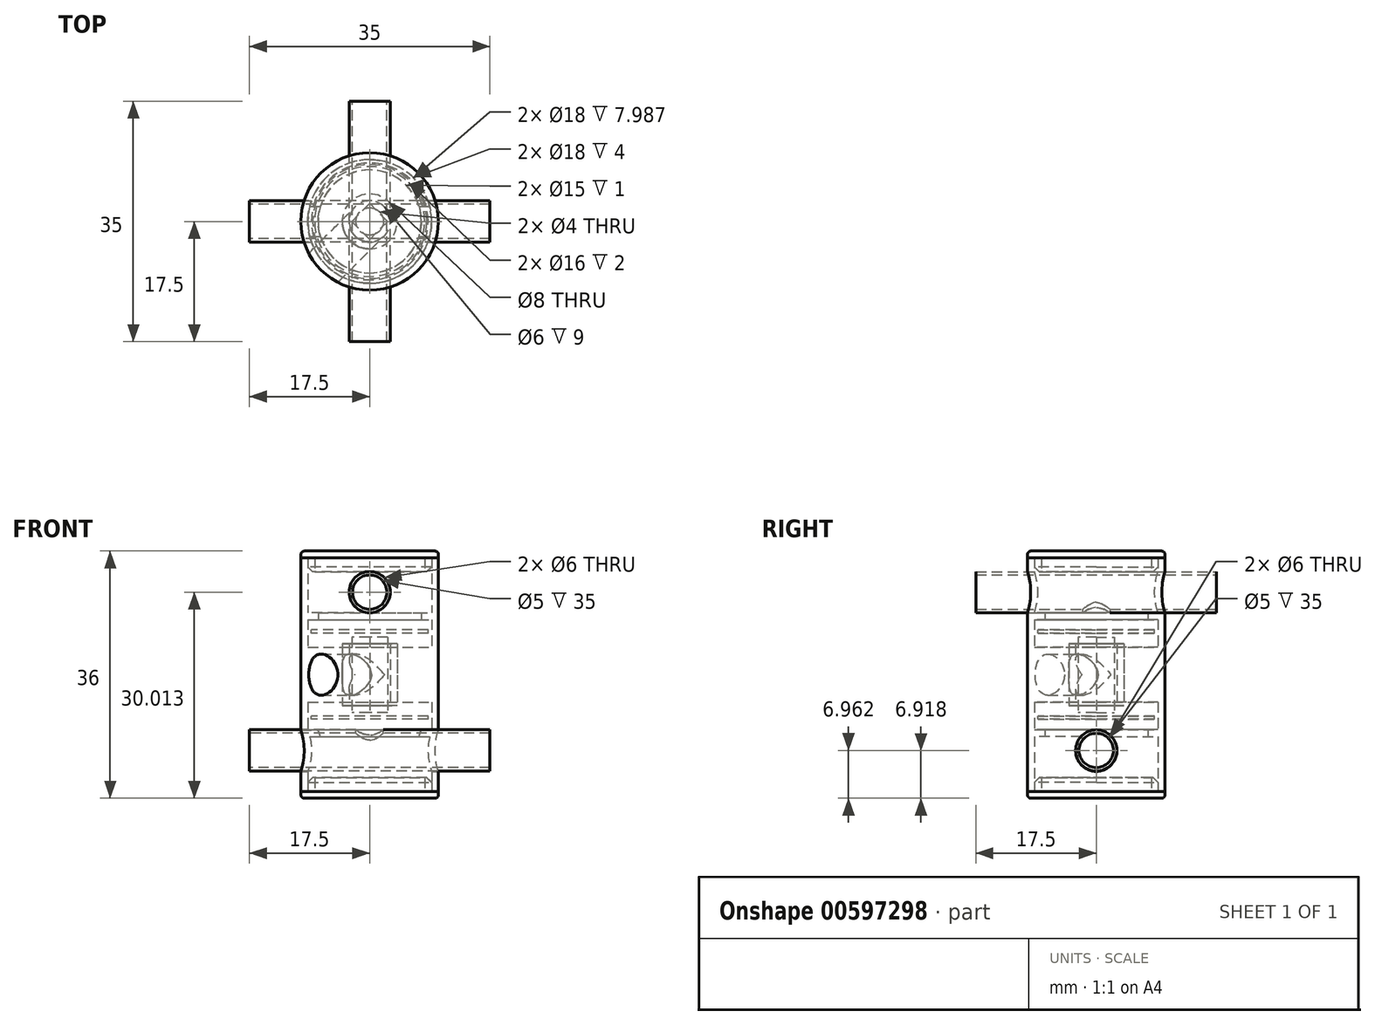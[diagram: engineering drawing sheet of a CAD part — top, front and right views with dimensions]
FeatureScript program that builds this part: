
annotation { "Feature Type Name" : "Feature", "Feature Type Description" : "" }
export const myFeature = defineFeature(function(context is Context, id is Id, definition is map)
    precondition{}
    {
        {
            var Q0;
            Q0=qCreatedBy(makeId("Front.planeOp"),FACE);
            var sketch = newSketch(context, id + "F0", { "sketchPlane" : qUnion([Q0])});
            skLineSegment(sketch, "E0.top", {"start": v(0, 15) * mm, "end": v(-30, 15) * mm});
            skLineSegment(sketch, "E1", {"start": v(0, 30) * mm, "end": v(0, 36) * mm});
            skLineSegment(sketch, "E2", {"start": v(0, 0) * mm, "end": v(0, -6) * mm});
            skSolve(sketch);
        }
        {
            var Q0;
            Q0=qCreatedBy(makeId("Front.planeOp"),FACE);
            var sketch = newSketch(context, id + "F1", { "sketchPlane" : qUnion([Q0])});
            skLineSegment(sketch, "E3.bottom", {"start": v(4, 19.01) * mm, "end": v(9, 19.01) * mm});
            skLineSegment(sketch, "E3.top", {"start": v(4, 10.99) * mm, "end": v(9, 10.99) * mm});
            skLineSegment(sketch, "E3.left", {"start": v(4, 19.01) * mm, "end": v(4, 10.99) * mm});
            skLineSegment(sketch, "E3.right", {"start": v(9, 19.01) * mm, "end": v(9, 10.99) * mm});
            skLineSegment(sketch, "E4.bottom", {"start": v(9, 32) * mm, "end": v(10, 32) * mm});
            skLineSegment(sketch, "E4.top", {"start": v(9, -2) * mm, "end": v(10, -2) * mm});
            skLineSegment(sketch, "E4.left", {"start": v(9, 32) * mm, "end": v(9, -2) * mm});
            skLineSegment(sketch, "E4.right", {"start": v(10, 32) * mm, "end": v(10, -2) * mm});
            skLineSegment(sketch, "E5.bottom", {"start": v(7.5, 24.01) * mm, "end": v(9, 24.01) * mm});
            skLineSegment(sketch, "E5.top", {"start": v(7.5, 23.01) * mm, "end": v(9, 23.01) * mm});
            skLineSegment(sketch, "E5.left", {"start": v(7.5, 24.01) * mm, "end": v(7.5, 23.01) * mm});
            skLineSegment(sketch, "E6", {"start": v(9, 24.01) * mm, "end": v(9, 23.01) * mm});
            skLineSegment(sketch, "E7.MirrorCS", {"start": v(7.5, 6.99) * mm, "end": v(9, 6.99) * mm});
            skLineSegment(sketch, "E8.MirrorCS", {"start": v(7.5, 5.99) * mm, "end": v(7.5, 6.99) * mm});
            skLineSegment(sketch, "E9.MirrorCS", {"start": v(9, 5.99) * mm, "end": v(9, 6.99) * mm});
            skLineSegment(sketch, "E10.MirrorCS", {"start": v(7.5, 5.99) * mm, "end": v(9, 5.99) * mm});
            skSolve(sketch);
        }
        {
            var Q0;
            Q0=qCreatedBy(makeId("Front.planeOp"),FACE);
            var sketch = newSketch(context, id + "F2", { "sketchPlane" : qUnion([Q0])});
            skLineSegment(sketch, "E11.bottom", {"start": v(0, 21.51) * mm, "end": v(8.5, 21.51) * mm});
            skLineSegment(sketch, "E11.top", {"start": v(0, 21.01) * mm, "end": v(8.5, 21.01) * mm});
            skLineSegment(sketch, "E11.left", {"start": v(0, 21.51) * mm, "end": v(0, 21.01) * mm});
            skLineSegment(sketch, "E11.right", {"start": v(8.5, 21.51) * mm, "end": v(8.5, 21.01) * mm});
            skLineSegment(sketch, "E12.MirrorCS", {"start": v(0, 8.99) * mm, "end": v(8.5, 8.99) * mm});
            skLineSegment(sketch, "E13.MirrorCS", {"start": v(0, 8.49) * mm, "end": v(8.5, 8.49) * mm});
            skLineSegment(sketch, "E14.MirrorCS", {"start": v(0, 8.49) * mm, "end": v(0, 8.99) * mm});
            skLineSegment(sketch, "E15.MirrorCS", {"start": v(8.5, 8.49) * mm, "end": v(8.5, 8.99) * mm});
            skSolve(sketch);
        }
        {
            var Q0;
            Q0=makeQuery(id+"F2.imprint","IMPRINT",FACE,{"disambiguationData":[TD([[makeQuery(id+"F2.imprint","IMPRINT",EDGE,{"derivedFrom":sQuery(id+"F2.wireOp",EDGE,"E12.MirrorCS")}),-1.0]])]});
            var Q1;
            Q1=makeQuery(id+"F2.imprint","IMPRINT",FACE,{"disambiguationData":[TD([[makeQuery(id+"F2.imprint","IMPRINT",EDGE,{"derivedFrom":sQuery(id+"F2.wireOp",EDGE,"E11.bottom")}),-1.0]])]});
            var Q2;
            Q2=sQuery(id+"F2.wireOp",EDGE,"E11.left");
            revolve(context, id + "F3", {"entities" : qUnion([Q0, Q1]), "axis" : qUnion([Q2]), "revolveType" : RevolveType.FULL});
        }
        {
            var Q0;
            Q0 = qSketchRegion(id + "F1", true);
            var Q1;
            Q1=sQuery(id+"F0.wireOp",EDGE,"E1");
            revolve(context, id + "F4", {"entities" : qUnion([Q0]), "axis" : qUnion([Q1]), "revolveType" : RevolveType.FULL});
        }
        {
            var Q0;
            Q0=qCreatedBy(makeId("Front.planeOp"),FACE);
            var sketch = newSketch(context, id + "F5", { "sketchPlane" : qUnion([Q0])});
            skCircle(sketch, "E16", {"center": v(0, 27.01) * mm, "radius": 3 * mm});
            skLineSegment(sketch, "E17.bottom", {"start": v(4, 10.51) * mm, "end": v(3, 10.51) * mm});
            skLineSegment(sketch, "E17.top", {"start": v(4, 19.51) * mm, "end": v(3, 19.51) * mm});
            skLineSegment(sketch, "E17.left", {"start": v(4, 10.51) * mm, "end": v(4, 19.51) * mm});
            skLineSegment(sketch, "E17.right", {"start": v(3, 10.51) * mm, "end": v(3, 19.51) * mm});
            skPoint(sketch, "E17.middle", {"position": v(0, 15.01) * mm});
            skSolve(sketch);
        }
        {
            var Q0;
            Q0=makeQuery(id+"F5.imprint","IMPRINT",FACE,{"disambiguationData":[TD([[makeQuery(id+"F5.imprint","IMPRINT",EDGE,{"derivedFrom":sQuery(id+"F5.wireOp",EDGE,"E16")}),1.0]])]});
            extrude(context, id + "F6", {"entities" : qUnion([Q0]), "operationType" : NewBodyOperationType.REMOVE, "endBound" : BoundingType.SYMMETRIC, "depth" : 25 * mm, "offsetDistance" : 25 * mm});
        }
        {
            var Q0;
            Q0=makeQuery(id+"F5.imprint","IMPRINT",FACE,{"disambiguationData":[TD([[makeQuery(id+"F5.imprint","IMPRINT",EDGE,{"derivedFrom":sQuery(id+"F5.wireOp",EDGE,"E17.bottom")}),-1.0]])]});
            var Q1;
            Q1=sQuery(id+"F0.wireOp",EDGE,"E1");
            revolve(context, id + "F7", {"entities" : qUnion([Q0]), "axis" : qUnion([Q1]), "revolveType" : RevolveType.FULL});
        }
        {
            var Q0;
            Q0=makeQuery(id+"F3.opRevolve","SWEPT_FACE",FACE,{"disambiguationData":[OSD([sQuery(id+"F2.wireOp",EDGE,"E12.MirrorCS")])]});
            var sketch = newSketch(context, id + "F8", { "sketchPlane" : qUnion([Q0])});
            skSolve(sketch);
        }
        {
            var Q0;
            Q0=makeQuery(id+"F8.imprint","IMPRINT",FACE,{"disambiguationData":[TD([[makeQuery(id+"F8.imprint","IMPRINT",EDGE,{"derivedFrom":makeQuery(id+"F3.opRevolve","SWEPT_EDGE",EDGE,{"disambiguationData":[OSD([sQuery(id+"F2.wireOp",EDGE,"E12.MirrorCS"),sQuery(id+"F2.wireOp",EDGE,"E15.MirrorCS")])]})}),1.0]])]});
            var sketch = newSketch(context, id + "F9", { "sketchPlane" : qUnion([Q0])});
            skLineSegment(sketch, "E18.bottom", {"start": v(-16.44, -8.27) * mm, "end": v(-23.88, -8.27) * mm});
            skLineSegment(sketch, "E18.top", {"start": v(-16.44, -1.54) * mm, "end": v(-23.88, -1.54) * mm});
            skLineSegment(sketch, "E18.left", {"start": v(-16.44, -8.27) * mm, "end": v(-16.44, -1.54) * mm});
            skLineSegment(sketch, "E18.right", {"start": v(-23.88, -8.27) * mm, "end": v(-23.88, -1.54) * mm});
            skPoint(sketch, "E18.middle", {"position": v(-20.16, -4.9) * mm});
            skSolve(sketch);
        }
        {
            var Q0;
            Q0 = qSketchRegion(id + "F9", true);
            extrude(context, id + "F10", {"entities" : qUnion([Q0]), "depth" : 0.5 * mm, "offsetDistance" : 25 * mm});
        }
        {
            var Q0;
            Q0=makeQuery(id+"F10.opExtrude","CAP_FACE",FACE,{"disambiguationData":[OSD([sQuery(id+"F9.wireOp",EDGE,"E18.bottom"),sQuery(id+"F9.wireOp",EDGE,"E18.top"),sQuery(id+"F9.wireOp",EDGE,"E18.left"),sQuery(id+"F9.wireOp",EDGE,"E18.right")])],"isStart":false});
            var sketch = newSketch(context, id + "F11", { "sketchPlane" : qUnion([Q0])});
            skLineSegment(sketch, "E19.bottom", {"start": v(1.85, -1.85) * mm, "end": v(-1.85, -1.85) * mm});
            skLineSegment(sketch, "E19.top", {"start": v(1.85, 1.85) * mm, "end": v(-1.85, 1.85) * mm});
            skLineSegment(sketch, "E19.left", {"start": v(1.85, -1.85) * mm, "end": v(1.85, 1.85) * mm});
            skLineSegment(sketch, "E19.right", {"start": v(-1.85, -1.85) * mm, "end": v(-1.85, 1.85) * mm});
            skPoint(sketch, "E19.middle", {"position": v(0, 0) * mm});
            skSolve(sketch);
        }
        {
            var Q0;
            Q0=makeQuery(id+"F11.imprint","IMPRINT",FACE,{"disambiguationData":[TD([[makeQuery(id+"F11.imprint","IMPRINT",EDGE,{"derivedFrom":sQuery(id+"F11.wireOp",EDGE,"E19.bottom")}),-1.0]])]});
            extrude(context, id + "F12", {"entities" : qUnion([Q0]), "operationType" : NewBodyOperationType.ADD, "depth" : 11 * mm, "offsetDistance" : 25 * mm});
        }
        {
            var Q0;
            Q0=makeQuery(id+"F10.opExtrude","SWEPT_BODY",BODY,{"disambiguationData":[OSD([sQuery(id+"F9.wireOp",EDGE,"E18.bottom"),sQuery(id+"F9.wireOp",EDGE,"E18.top"),sQuery(id+"F9.wireOp",EDGE,"E18.left"),sQuery(id+"F9.wireOp",EDGE,"E18.right")])]});
            deleteBodies(context, id + "F13", {"entities" : qUnion([Q0])});
        }
        {
            var Q0;
            Q0=qCreatedBy(makeId("Right.planeOp"),FACE);
            var sketch = newSketch(context, id + "F14", { "sketchPlane" : qUnion([Q0])});
            skCircle(sketch, "E20", {"center": v(0, 3.92) * mm, "radius": 3 * mm});
            skSolve(sketch);
        }
        {
            var Q0;
            Q0=makeQuery(id+"F14.imprint","IMPRINT",FACE,{"disambiguationData":[TD([[makeQuery(id+"F14.imprint","IMPRINT",EDGE,{"derivedFrom":sQuery(id+"F14.wireOp",EDGE,"E20")}),1.0]])]});
            extrude(context, id + "F15", {"entities" : qUnion([Q0]), "operationType" : NewBodyOperationType.REMOVE, "endBound" : BoundingType.SYMMETRIC, "oppositeDirection" : true, "depth" : 125 * mm, "offsetDistance" : 25 * mm});
        }
        {
            var Q0;
            Q0=makeQuery(id+"F12.opExtrude","SWEPT_BODY",BODY,{"disambiguationData":[OSD([sQuery(id+"F11.wireOp",EDGE,"E19.bottom"),sQuery(id+"F11.wireOp",EDGE,"E19.top"),sQuery(id+"F11.wireOp",EDGE,"E19.left"),sQuery(id+"F11.wireOp",EDGE,"E19.right")])]});
            var Q1;
            Q1=sQuery(id+"F0.wireOp",EDGE,"E1");
            transform(context, id + "F16", {"entities" : qUnion([Q0]), "transformType" : TransformType.ROTATION, "transformAxis" : qUnion([Q1]), "angle" : 45 * degree, "makeCopy" : false});
        }
        {
            var Q0;
            Q0=makeQuery(id+"F7.opRevolve","SWEPT_BODY",BODY,{"disambiguationData":[OSD([sQuery(id+"F5.wireOp",EDGE,"E17.bottom"),sQuery(id+"F5.wireOp",EDGE,"E17.top"),sQuery(id+"F5.wireOp",EDGE,"E17.left"),sQuery(id+"F5.wireOp",EDGE,"E17.right")])]});
            var Q1;
            Q1=sQuery(id+"F0.wireOp",EDGE,"E1");
            transform(context, id + "F17", {"entities" : qUnion([Q0]), "transformType" : TransformType.ROTATION, "transformAxis" : qUnion([Q1]), "angle" : 45 * degree, "oppositeDirection" : true, "makeCopy" : false});
        }
        {
            var Q0;
            Q0=makeQuery(id+"F12.opExtrude","SWEPT_FACE",FACE,{"disambiguationData":[OSD([sQuery(id+"F11.wireOp",EDGE,"E19.right")])]});
            var sketch = newSketch(context, id + "F18", { "sketchPlane" : qUnion([Q0])});
            skCircle(sketch, "E21", {"center": v(0, 15) * mm, "radius": 3 * mm});
            skSolve(sketch);
        }
        {
            var Q0;
            {var subQ0=sQuery(id+"F18.wireOp",EDGE,"E21");var subQ1=makeQuery(id+"F12.opExtrude","SWEPT_EDGE",EDGE,{"disambiguationData":[OSD([sQuery(id+"F11.wireOp",EDGE,"E19.top"),sQuery(id+"F11.wireOp",EDGE,"E19.right")])]});var subQ2=makeQuery(id+"F18.imprint","INTERSECT",VERTEX,{"disambiguationData":[OD(0.0)],"derivedFrom":[subQ1,subQ0]});Q0=makeQuery(id+"F18.imprint","IMPRINT",FACE,{"disambiguationData":[TD([[makeQuery(id+"F18.imprint","IMPRINT",EDGE,{"disambiguationData":[TD([[subQ2,-1.0]])],"derivedFrom":subQ0}),1.0]])]});}
            var Q1;
            {var subQ0=sQuery(id+"F18.wireOp",EDGE,"E21");var subQ1=sQuery(id+"F11.wireOp",EDGE,"E19.right");var subQ2=makeQuery(id+"F12.opExtrude","SWEPT_EDGE",EDGE,{"disambiguationData":[OSD([sQuery(id+"F11.wireOp",EDGE,"E19.top"),subQ1])]});var subQ3=makeQuery(id+"F18.imprint","INTERSECT",VERTEX,{"disambiguationData":[OD(0.0)],"derivedFrom":[subQ2,subQ0]});Q1=makeQuery(id+"F18.imprint","IMPRINT",FACE,{"disambiguationData":[TD([[makeQuery(id+"F18.imprint","IMPRINT",EDGE,{"disambiguationData":[TD([[subQ3,1.0]])],"derivedFrom":subQ0}),1.0]])]});}
            var Q2;
            {var subQ0=sQuery(id+"F18.wireOp",EDGE,"E21");var subQ1=makeQuery(id+"F12.opExtrude","SWEPT_EDGE",EDGE,{"disambiguationData":[OSD([sQuery(id+"F11.wireOp",EDGE,"E19.bottom"),sQuery(id+"F11.wireOp",EDGE,"E19.right")])]});var subQ2=makeQuery(id+"F18.imprint","INTERSECT",VERTEX,{"disambiguationData":[OD(0.0)],"derivedFrom":[subQ1,subQ0]});Q2=makeQuery(id+"F18.imprint","IMPRINT",FACE,{"disambiguationData":[TD([[makeQuery(id+"F18.imprint","IMPRINT",EDGE,{"disambiguationData":[TD([[subQ2,1.0]])],"derivedFrom":subQ0}),1.0]])]});}
            extrude(context, id + "F19", {"entities" : qUnion([Q0, Q1, Q2]), "operationType" : NewBodyOperationType.REMOVE, "depth" : 25 * mm, "offsetDistance" : 25 * mm});
        }
        {
            var Q0;
            Q0=makeQuery(id+"F19.boolean.opBoolean","COPY",FACE,{"disambiguationData":[OD(0.0)],"derivedFrom":makeQuery(id+"F19.opExtrude","CAP_FACE",FACE,{"disambiguationData":[OSD([sQuery(id+"F18.wireOp",EDGE,"E21")])],"isStart":true})});
            var Q1;
            Q1=makeQuery(id+"F19.boolean.opBoolean","COPY",FACE,{"disambiguationData":[OD(1.0)],"derivedFrom":makeQuery(id+"F19.opExtrude","CAP_FACE",FACE,{"disambiguationData":[OSD([sQuery(id+"F18.wireOp",EDGE,"E21")])],"isStart":true})});
            extrude(context, id + "F20", {"entities" : qUnion([Q0, Q1]), "operationType" : NewBodyOperationType.REMOVE, "oppositeDirection" : true, "depth" : 1.8 * mm, "offsetDistance" : 25 * mm});
        }
        {
            var Q0;
            {var subQ0=sQuery(id+"F18.wireOp",EDGE,"E21");var subQ1=sQuery(id+"F11.wireOp",EDGE,"E19.right");var subQ2=makeQuery(id+"F12.opExtrude","SWEPT_EDGE",EDGE,{"disambiguationData":[OSD([sQuery(id+"F11.wireOp",EDGE,"E19.top"),subQ1])]});var subQ3=makeQuery(id+"F18.imprint","INTERSECT",VERTEX,{"disambiguationData":[OD(0.0)],"derivedFrom":[subQ2,subQ0]});Q0=makeQuery(id+"F18.imprint","IMPRINT",FACE,{"disambiguationData":[TD([[makeQuery(id+"F18.imprint","IMPRINT",EDGE,{"disambiguationData":[TD([[subQ3,1.0]])],"derivedFrom":subQ0}),1.0]])]});}
            var Q1;
            {var subQ0=sQuery(id+"F18.wireOp",EDGE,"E21");var subQ1=makeQuery(id+"F12.opExtrude","SWEPT_EDGE",EDGE,{"disambiguationData":[OSD([sQuery(id+"F11.wireOp",EDGE,"E19.top"),sQuery(id+"F11.wireOp",EDGE,"E19.right")])]});var subQ2=makeQuery(id+"F18.imprint","INTERSECT",VERTEX,{"disambiguationData":[OD(0.0)],"derivedFrom":[subQ1,subQ0]});Q1=makeQuery(id+"F18.imprint","IMPRINT",FACE,{"disambiguationData":[TD([[makeQuery(id+"F18.imprint","IMPRINT",EDGE,{"disambiguationData":[TD([[subQ2,-1.0]])],"derivedFrom":subQ0}),1.0]])]});}
            var Q2;
            {var subQ0=sQuery(id+"F18.wireOp",EDGE,"E21");var subQ1=makeQuery(id+"F12.opExtrude","SWEPT_EDGE",EDGE,{"disambiguationData":[OSD([sQuery(id+"F11.wireOp",EDGE,"E19.bottom"),sQuery(id+"F11.wireOp",EDGE,"E19.right")])]});var subQ2=makeQuery(id+"F18.imprint","INTERSECT",VERTEX,{"disambiguationData":[OD(0.0)],"derivedFrom":[subQ1,subQ0]});Q2=makeQuery(id+"F18.imprint","IMPRINT",FACE,{"disambiguationData":[TD([[makeQuery(id+"F18.imprint","IMPRINT",EDGE,{"disambiguationData":[TD([[subQ2,1.0]])],"derivedFrom":subQ0}),1.0]])]});}
            extrude(context, id + "F21", {"entities" : qUnion([Q0, Q1, Q2]), "operationType" : NewBodyOperationType.REMOVE, "depth" : 25 * mm, "offsetDistance" : 25 * mm});
        }
        {
            var Q0;
            Q0=qCreatedBy(makeId("Front.planeOp"),FACE);
            var sketch = newSketch(context, id + "F22", { "sketchPlane" : qUnion([Q0])});
            skLineSegment(sketch, "E22.top", {"start": v(10, 33) * mm, "end": v(0, 33) * mm});
            skLineSegment(sketch, "E22.left", {"start": v(10, 32) * mm, "end": v(10, 33) * mm});
            skLineSegment(sketch, "E22.right", {"start": v(0, 32) * mm, "end": v(0, 33) * mm});
            skLineSegment(sketch, "E23.top", {"start": v(9, 30) * mm, "end": v(8, 30) * mm});
            skLineSegment(sketch, "E23.left", {"start": v(9, 32) * mm, "end": v(9, 30) * mm});
            skLineSegment(sketch, "E23.right", {"start": v(8, 32) * mm, "end": v(8, 30) * mm});
            skLineSegment(sketch, "E24", {"start": v(8, 32) * mm, "end": v(0, 32) * mm});
            skLineSegment(sketch, "E25", {"start": v(9, 32) * mm, "end": v(10, 32) * mm});
            skLineSegment(sketch, "E26.MirrorCS", {"start": v(9, -2) * mm, "end": v(10, -2) * mm});
            skLineSegment(sketch, "E27.MirrorCS", {"start": v(10, -2) * mm, "end": v(10, -3) * mm});
            skLineSegment(sketch, "E28.MirrorCS", {"start": v(9, 0) * mm, "end": v(8, 0) * mm});
            skLineSegment(sketch, "E29.MirrorCS", {"start": v(0, -2) * mm, "end": v(0, -3) * mm});
            skLineSegment(sketch, "E30.MirrorCS", {"start": v(10, -3) * mm, "end": v(0, -3) * mm});
            skLineSegment(sketch, "E31.MirrorCS", {"start": v(8, -2) * mm, "end": v(8, 0) * mm});
            skLineSegment(sketch, "E32.MirrorCS", {"start": v(8, -2) * mm, "end": v(0, -2) * mm});
            skLineSegment(sketch, "E33.MirrorCS", {"start": v(9, -2) * mm, "end": v(9, 0) * mm});
            skSolve(sketch);
        }
        {
            var Q0;
            Q0=makeQuery(id+"F22.imprint","IMPRINT",FACE,{"disambiguationData":[TD([[makeQuery(id+"F22.imprint","IMPRINT",EDGE,{"derivedFrom":sQuery(id+"F22.wireOp",EDGE,"E22.top")}),1.0]])]});
            var Q1;
            Q1=makeQuery(id+"F22.imprint","IMPRINT",FACE,{"disambiguationData":[TD([[makeQuery(id+"F22.imprint","IMPRINT",EDGE,{"derivedFrom":sQuery(id+"F22.wireOp",EDGE,"E26.MirrorCS")}),-1.0]])]});
            var Q2;
            Q2=sQuery(id+"F0.wireOp",EDGE,"E1");
            revolve(context, id + "F23", {"entities" : qUnion([Q0, Q1]), "axis" : qUnion([Q2]), "revolveType" : RevolveType.FULL});
        }
        {
            var Q0;
            Q0=makeQuery(id+"F23.opRevolve","SWEPT_EDGE",EDGE,{"disambiguationData":[OSD([sQuery(id+"F22.wireOp",EDGE,"E22.top"),sQuery(id+"F22.wireOp",EDGE,"E22.left")])]});
            var Q1;
            Q1=makeQuery(id+"F23.opRevolve","SWEPT_EDGE",EDGE,{"disambiguationData":[OSD([sQuery(id+"F22.wireOp",EDGE,"E27.MirrorCS"),sQuery(id+"F22.wireOp",EDGE,"E30.MirrorCS")])]});
            fillet(context, id + "F24", {"entities" : qUnion([Q0, Q1]), "radius" : 0.5 * mm, "tangentPropagation" : true, "allowEdgeOverflow" : false});
        }
        {
            var Q0;
            Q0=makeQuery(id+"F23.opRevolve","SWEPT_EDGE",EDGE,{"disambiguationData":[OSD([sQuery(id+"F22.wireOp",EDGE,"E23.top"),sQuery(id+"F22.wireOp",EDGE,"E23.left")])]});
            var Q1;
            Q1=makeQuery(id+"F23.opRevolve","SWEPT_EDGE",EDGE,{"disambiguationData":[OSD([sQuery(id+"F22.wireOp",EDGE,"E28.MirrorCS"),sQuery(id+"F22.wireOp",EDGE,"E33.MirrorCS")])]});
            chamfer(context, id + "F25", {"entities" : qUnion([Q0, Q1]), "width" : 0.7 * mm, "tangentPropagation" : true});
        }
        {
            var Q0;
            Q0=qCreatedBy(makeId("Front.planeOp"),FACE);
            var sketch = newSketch(context, id + "F26", { "sketchPlane" : qUnion([Q0])});
            skCircle(sketch, "E34", {"center": v(0, 27.01) * mm, "radius": 3 * mm});
            skCircle(sketch, "E35", {"center": v(0, 27.01) * mm, "radius": 2.5 * mm});
            skSolve(sketch);
        }
        {
            var Q0;
            Q0=makeQuery(id+"F26.imprint","IMPRINT",FACE,{"disambiguationData":[TD([[makeQuery(id+"F26.imprint","IMPRINT",EDGE,{"derivedFrom":sQuery(id+"F26.wireOp",EDGE,"E34")}),1.0]])]});
            extrude(context, id + "F27", {"entities" : qUnion([Q0]), "endBound" : BoundingType.SYMMETRIC, "depth" : 35 * mm, "offsetDistance" : 25 * mm});
        }
        {
            var Q0;
            Q0=makeQuery(id+"F3.opRevolve","SWEPT_FACE",FACE,{"disambiguationData":[OSD([sQuery(id+"F2.wireOp",EDGE,"E11.bottom")])]});
            var sketch = newSketch(context, id + "F28", { "sketchPlane" : qUnion([Q0])});
            skCircle(sketch, "E36", {"center": v(0, 0) * mm, "radius": 2 * mm});
            skSolve(sketch);
        }
        {
            var Q0;
            Q0=makeQuery(id+"F28.imprint","IMPRINT",FACE,{"disambiguationData":[TD([[makeQuery(id+"F28.imprint","IMPRINT",EDGE,{"derivedFrom":sQuery(id+"F28.wireOp",EDGE,"E36")}),1.0]])]});
            extrude(context, id + "F29", {"entities" : qUnion([Q0]), "operationType" : NewBodyOperationType.REMOVE, "depth" : 5 * mm, "offsetDistance" : 25 * mm});
        }
        {
            var Q0;
            Q0=makeQuery(id+"F27.opExtrude","SWEPT_BODY",BODY,{"disambiguationData":[OSD([sQuery(id+"F26.wireOp",EDGE,"E34"),sQuery(id+"F26.wireOp",EDGE,"E35")])]});
            var Q1;
            Q1=makeQuery(id+"F3.opRevolve","SWEPT_FACE",FACE,{"disambiguationData":[OSD([sQuery(id+"F2.wireOp",EDGE,"E13.MirrorCS")])]});
            mirror(context, id + "F30", {"entities" : qUnion([Q0]), "mirrorPlane" : qUnion([Q1])});
        }
        {
            var Q0;
            Q0=makeQuery(id+"F30.opPattern","COPY",BODY,{"derivedFrom":makeQuery(id+"F27.opExtrude","SWEPT_BODY",BODY,{"disambiguationData":[OSD([sQuery(id+"F26.wireOp",EDGE,"E34"),sQuery(id+"F26.wireOp",EDGE,"E35")])]}),"instanceName":"1"});
            var Q1;
            Q1=sQuery(id+"F0.wireOp",EDGE,"E1");
            transform(context, id + "F31", {"entities" : qUnion([Q0]), "transformType" : TransformType.ROTATION, "transformAxis" : qUnion([Q1]), "angle" : 90 * degree, "makeCopy" : false});
        }
        {
            var Q0;
            Q0=makeQuery(id+"F30.opPattern","COPY",BODY,{"derivedFrom":makeQuery(id+"F27.opExtrude","SWEPT_BODY",BODY,{"disambiguationData":[OSD([sQuery(id+"F26.wireOp",EDGE,"E34"),sQuery(id+"F26.wireOp",EDGE,"E35")])]}),"instanceName":"1"});
            var Q1;
            Q1=sQuery(id+"F0.wireOp",EDGE,"E2");
            transform(context, id + "F32", {"entities" : qUnion([Q0]), "transformType" : TransformType.TRANSLATION_DISTANCE, "transformDirection" : qUnion([Q1]), "distance" : 14 * mm, "oppositeDirection" : true, "makeCopy" : false});
        }
    });
